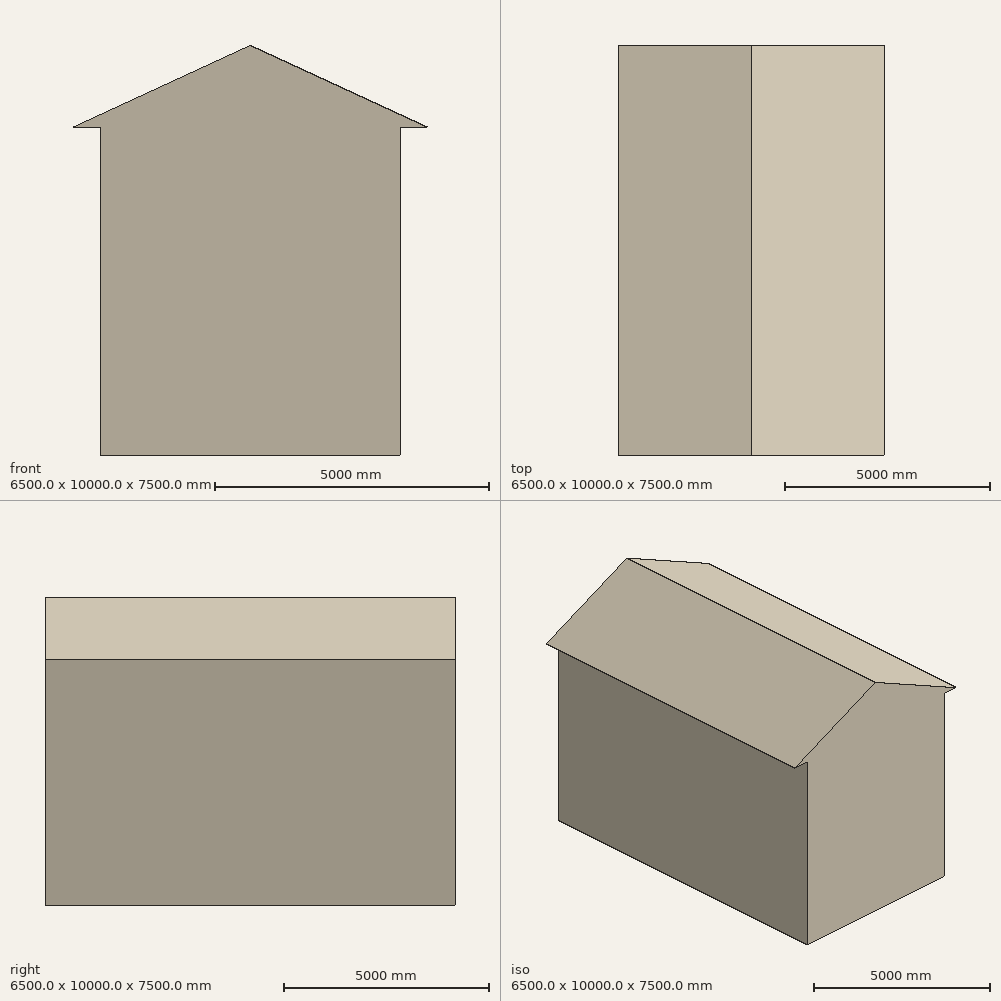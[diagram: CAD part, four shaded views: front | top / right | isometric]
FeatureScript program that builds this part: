
annotation { "Feature Type Name" : "Feature", "Feature Type Description" : "" }
export const myFeature = defineFeature(function(context is Context, id is Id, definition is map)
    precondition{}
    {
        {
            var Q0;
            Q0=qCreatedBy(makeId("Right.planeOp"),FACE);
            var sketch = newSketch(context, id + "F0", { "sketchPlane" : qUnion([Q0])});
            skLineSegment(sketch, "E0.bottom", {"start": v(0, 0) * mm, "end": v(10000, 0) * mm});
            skLineSegment(sketch, "E0.top", {"start": v(0, 6000) * mm, "end": v(10000, 6000) * mm});
            skLineSegment(sketch, "E0.left", {"start": v(0, 0) * mm, "end": v(0, 6000) * mm});
            skLineSegment(sketch, "E0.right", {"start": v(10000, 0) * mm, "end": v(10000, 6000) * mm});
            skSolve(sketch);
        }
        {
            var Q0;
            Q0=makeQuery(id+"F0.imprint","IMPRINT",FACE,{"disambiguationData":[TD([[makeQuery(id+"F0.imprint","IMPRINT",EDGE,{"derivedFrom":sQuery(id+"F0.wireOp",EDGE,"E0.bottom")}),1.0]])]});
            extrude(context, id + "F1", {"entities" : qUnion([Q0]), "depth" : 5500 * mm, "offsetDistance" : 25 * mm});
        }
        {
            var Q0;
            Q0=makeQuery(id+"F1.opExtrude","SWEPT_FACE",FACE,{"disambiguationData":[OSD([sQuery(id+"F0.wireOp",EDGE,"E0.left")])]});
            var sketch = newSketch(context, id + "F2", { "sketchPlane" : qUnion([Q0])});
            skLineSegment(sketch, "E1", {"start": v(2750, 6000) * mm, "end": v(6000, 6000) * mm});
            skLineSegment(sketch, "E2", {"start": v(6000, 6000) * mm, "end": v(2750, 7500) * mm});
            skLineSegment(sketch, "E3", {"start": v(2750, 7500) * mm, "end": v(2750, 6000) * mm, "construction": true});
            skLineSegment(sketch, "E4.MirrorCS", {"start": v(-500, 6000) * mm, "end": v(2750, 7500) * mm});
            skLineSegment(sketch, "E5.MirrorCS", {"start": v(2750, 6000) * mm, "end": v(-500, 6000) * mm});
            skSolve(sketch);
        }
        {
            var Q0;
            {var subQ1=sQuery(id+"F2.wireOp",EDGE,"E2");Q0=makeQuery(id+"F2.imprint","IMPRINT",FACE,{"disambiguationData":[TD([[makeQuery(id+"F2.imprint","IMPRINT",EDGE,{"derivedFrom":subQ1}),1.0]])]});}
            var Q1;
            Q1=makeQuery(id+"F1.opExtrude","SWEPT_FACE",FACE,{"disambiguationData":[OSD([sQuery(id+"F0.wireOp",EDGE,"E0.right")])]});
            extrude(context, id + "F3", {"entities" : qUnion([Q0]), "operationType" : NewBodyOperationType.ADD, "endBound" : BoundingType.UP_TO_SURFACE, "oppositeDirection" : true, "depth" : 25 * mm, "endBoundEntityFace" : qUnion([Q1]), "offsetDistance" : 25 * mm});
        }
    });
